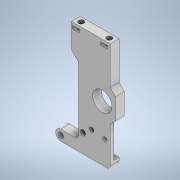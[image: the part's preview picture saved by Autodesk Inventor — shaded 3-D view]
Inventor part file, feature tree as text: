
AUTODESK INVENTOR PART (.ipt)
format: ipt  version: 2020.2 (Build 242310000, 310)  size: 264,704 bytes
history: native  units: mm
features: extrude x5, sketch x5, fillet x2, thread x2, mirror x1, projected_geometry x1
ambient origin geometry x8: Origin, YZ Plane, XZ Plane, XY Plane, X Axis, Y Axis, Z Axis, Center Point
bodies: Solid1 (feature_tree)
feature tree (16):
  extrude  "Extrusion1"  Depth=6.0mm
  fillet  "Fillet1"  Radius=28.0mm
  fillet  "Fillet2"  Radius=6.0mm
  extrude  "Extrusion2"  Depth=3.0mm
  extrude  "Extrusion3"  Depth=56.0mm
  thread  "Thread1"  [1 undecoded]
  thread  "Thread2"  [1 undecoded]
  mirror  "Mirror1"
  extrude  "Extrusion4"  Depth=12.5mm
  extrude  "Extrusion5"  Depth=2.0mm
  sketch  "Sketch1"  dims[d0=3.0mm d1=6.0mm d2=28.0mm d3=6.0mm]
  sketch  "Sketch2"  dims[d4=0.0mm d5=3.0mm]
  sketch  "Sketch3"  dims[d6=18.0mm d7=56.0mm d8=11.0mm d9=4.5mm]
  projected_geometry  "Projected Loop1"
  sketch  "Sketch5"  dims[d10=25.5mm d11=12.5mm]
  sketch  "Sketch6"  dims[d12=19.15mm d14=2.0mm d17=12.0mm d18=30.0mm d20=360.0deg d22=4.0mm d23=14.0mm d24=45.0deg d25=3.0mm d26=12.0mm d27=6.0mm d28=135.0deg d29=135.0deg d30=5.0mm d31=0.0mm d32=3.0mm d33=10.5mm d34=2.5mm d35=2.5mm d36=14.5mm d37=7.5mm d38=2.5mm d39=15.0mm d40=13.5mm d41=2.0mm d42=2.0mm d43=12.75mm d44=20.0mm d45=23.75mm d46=3.0mm d47=0.0mm d48=3.0mm d49=3.0mm d50=2.5mm d51=2.5mm d52=3.0mm d53=3.0mm d54=4.0mm d55=0.0mm d56=7.0mm d57=0.0mm d58=7.0mm d59=0.0mm d60=8.5mm d61=0.0mm d62=4.0mm d63=1.6mm d64=4.0mm d65=1.6mm d66=1.0mm d67=1.7mm d68=1.0mm d69=1.7mm d70=10.0mm d71=0.0mm d72=5.5mm d73=2.0mm d74=0.0mm]
note: 2 required parameter values undecoded (feature->parameter linkage not recoverable at this tier; creation-order binding heuristic only, values carry confidence <= 0.55)
